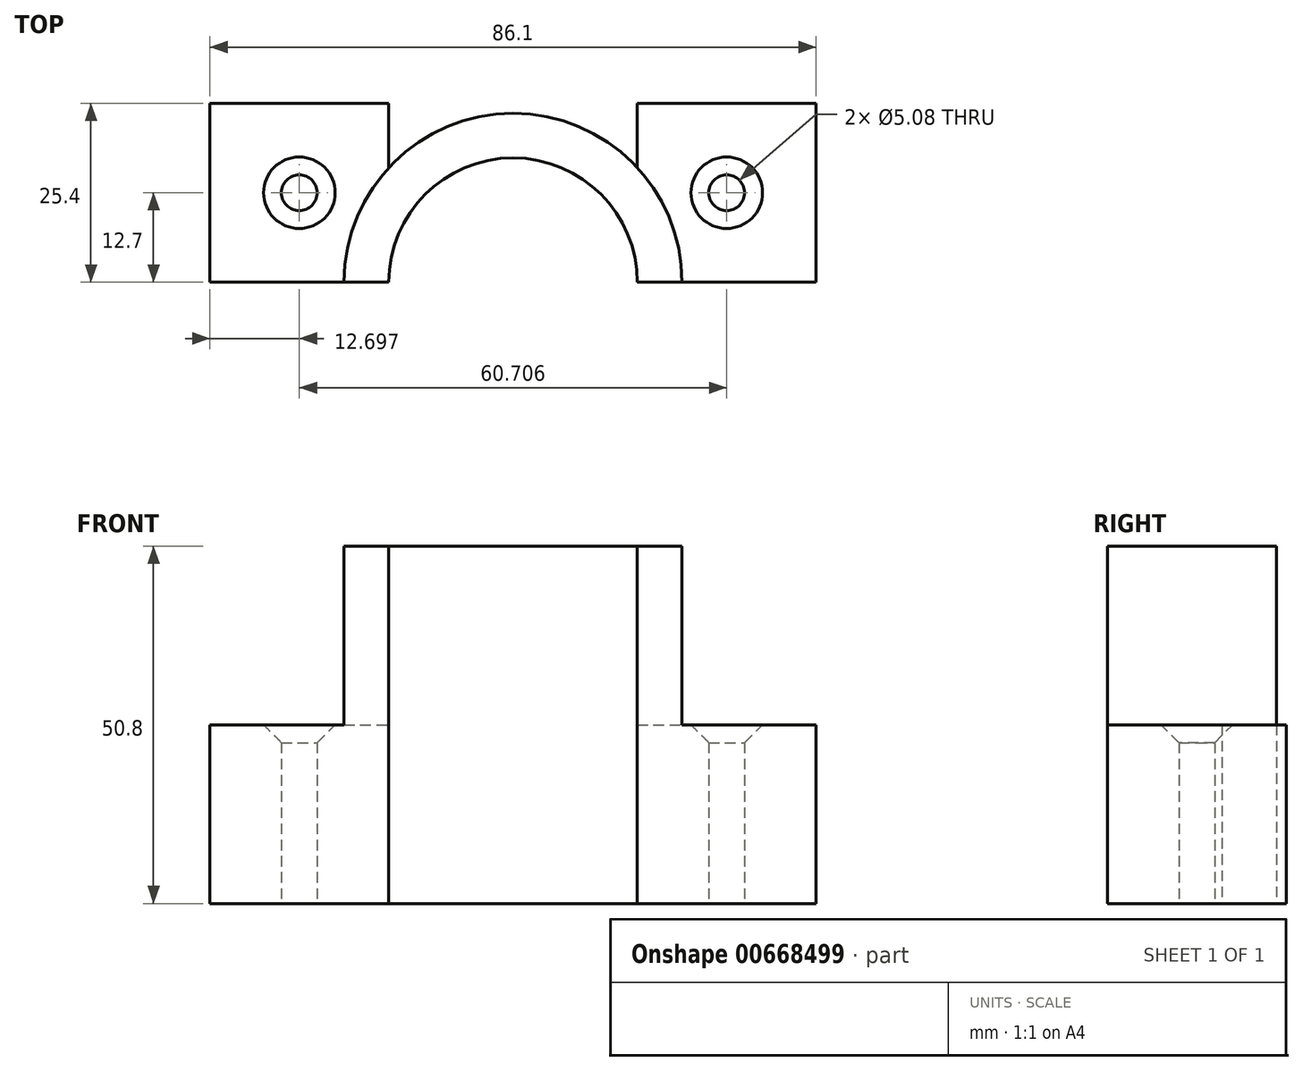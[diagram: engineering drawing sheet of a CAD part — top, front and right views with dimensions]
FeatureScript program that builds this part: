
annotation { "Feature Type Name" : "Feature", "Feature Type Description" : "" }
export const myFeature = defineFeature(function(context is Context, id is Id, definition is map)
    precondition{}
    {
        {
            var Q0;
            Q0=qCreatedBy(makeId("Front.planeOp"),FACE);
            var sketch = newSketch(context, id + "F0", { "sketchPlane" : qUnion([Q0])});
            skLineSegment(sketch, "E0.bottom", {"start": v(0, 0) * mm, "end": v(17.65, 0) * mm});
            skLineSegment(sketch, "E0.top", {"start": v(0, 50.8) * mm, "end": v(17.65, 50.8) * mm});
            skLineSegment(sketch, "E0.left", {"start": v(0, 0) * mm, "end": v(0, 50.8) * mm});
            skLineSegment(sketch, "E0.right", {"start": v(17.65, 0) * mm, "end": v(17.65, 50.8) * mm});
            skLineSegment(sketch, "E1.bottom", {"start": v(17.65, 0) * mm, "end": v(24, 0) * mm});
            skLineSegment(sketch, "E1.top", {"start": v(17.65, 50.8) * mm, "end": v(24, 50.8) * mm});
            skLineSegment(sketch, "E1.right", {"start": v(24, 0) * mm, "end": v(24, 50.8) * mm});
            skSolve(sketch);
        }
        {
            var Q0;
            Q0=makeQuery(id+"F0.imprint","IMPRINT",FACE,{"disambiguationData":[TD([[makeQuery(id+"F0.imprint","IMPRINT",EDGE,{"derivedFrom":sQuery(id+"F0.wireOp",EDGE,"E1.bottom")}),1.0]])]});
            var Q1;
            Q1=sQuery(id+"F0.wireOp",EDGE,"E0.left");
            revolve(context, id + "F1", {"surfaceOperationType" : NewSurfaceOperationType.NEW, "entities" : qUnion([Q0]), "axis" : qUnion([Q1]), "revolveType" : RevolveType.ONE_DIRECTION, "angle" : 180 * degree});
        }
        {
            var Q0;
            Q0=makeQuery(id+"F1.opRevolve","SWEPT_FACE",FACE,{"disambiguationData":[OSD([sQuery(id+"F0.wireOp",EDGE,"E1.bottom")])]});
            var sketch = newSketch(context, id + "F2", { "sketchPlane" : qUnion([Q0])});
            skLineSegment(sketch, "E2.bottom", {"start": v(17.65, 0) * mm, "end": v(43.05, 0) * mm});
            skLineSegment(sketch, "E2.top", {"start": v(17.65, -25.4) * mm, "end": v(43.05, -25.4) * mm});
            skLineSegment(sketch, "E2.left", {"start": v(17.65, 0) * mm, "end": v(17.65, -25.4) * mm});
            skLineSegment(sketch, "E2.right", {"start": v(43.05, 0) * mm, "end": v(43.05, -25.4) * mm});
            skLineSegment(sketch, "E3.bottom", {"start": v(-17.65, 0) * mm, "end": v(-43.05, 0) * mm});
            skLineSegment(sketch, "E3.top", {"start": v(-17.65, -25.4) * mm, "end": v(-43.05, -25.4) * mm});
            skLineSegment(sketch, "E3.left", {"start": v(-17.65, 0) * mm, "end": v(-17.65, -25.4) * mm});
            skLineSegment(sketch, "E3.right", {"start": v(-43.05, 0) * mm, "end": v(-43.05, -25.4) * mm});
            skCircle(sketch, "E4", {"center": v(30.35, -12.7) * mm, "radius": 2.54 * mm});
            skCircle(sketch, "E5", {"center": v(-30.35, -12.7) * mm, "radius": 2.54 * mm});
            skSolve(sketch);
        }
        {
            var Q0;
            {var subQ2=sQuery(id+"F2.wireOp",EDGE,"E2.top");Q0=makeQuery(id+"F2.imprint","IMPRINT",FACE,{"disambiguationData":[TD([[makeQuery(id+"F2.imprint","IMPRINT",EDGE,{"derivedFrom":subQ2}),1.0]])]});}
            var Q1;
            {var subQ2=sQuery(id+"F2.wireOp",EDGE,"E3.top");Q1=makeQuery(id+"F2.imprint","IMPRINT",FACE,{"disambiguationData":[TD([[makeQuery(id+"F2.imprint","IMPRINT",EDGE,{"derivedFrom":subQ2}),-1.0]])]});}
            extrude(context, id + "F3", {"entities" : qUnion([Q0, Q1]), "operationType" : NewBodyOperationType.ADD, "oppositeDirection" : true, "depth" : 25.4 * mm, "offsetDistance" : 25.4 * mm});
        }
        {
            var Q0;
            Q0=makeQuery(id+"F3.opExtrude","CAP_EDGE",EDGE,{"disambiguationData":[OSD([sQuery(id+"F2.wireOp",EDGE,"E5")])],"isStart":false});
            var Q1;
            Q1=makeQuery(id+"F3.opExtrude","CAP_EDGE",EDGE,{"disambiguationData":[OSD([sQuery(id+"F2.wireOp",EDGE,"E4")])],"isStart":false});
            chamfer(context, id + "F4", {"entities" : qUnion([Q0, Q1]), "width" : 2.54 * mm, "tangentPropagation" : true});
        }
    });
